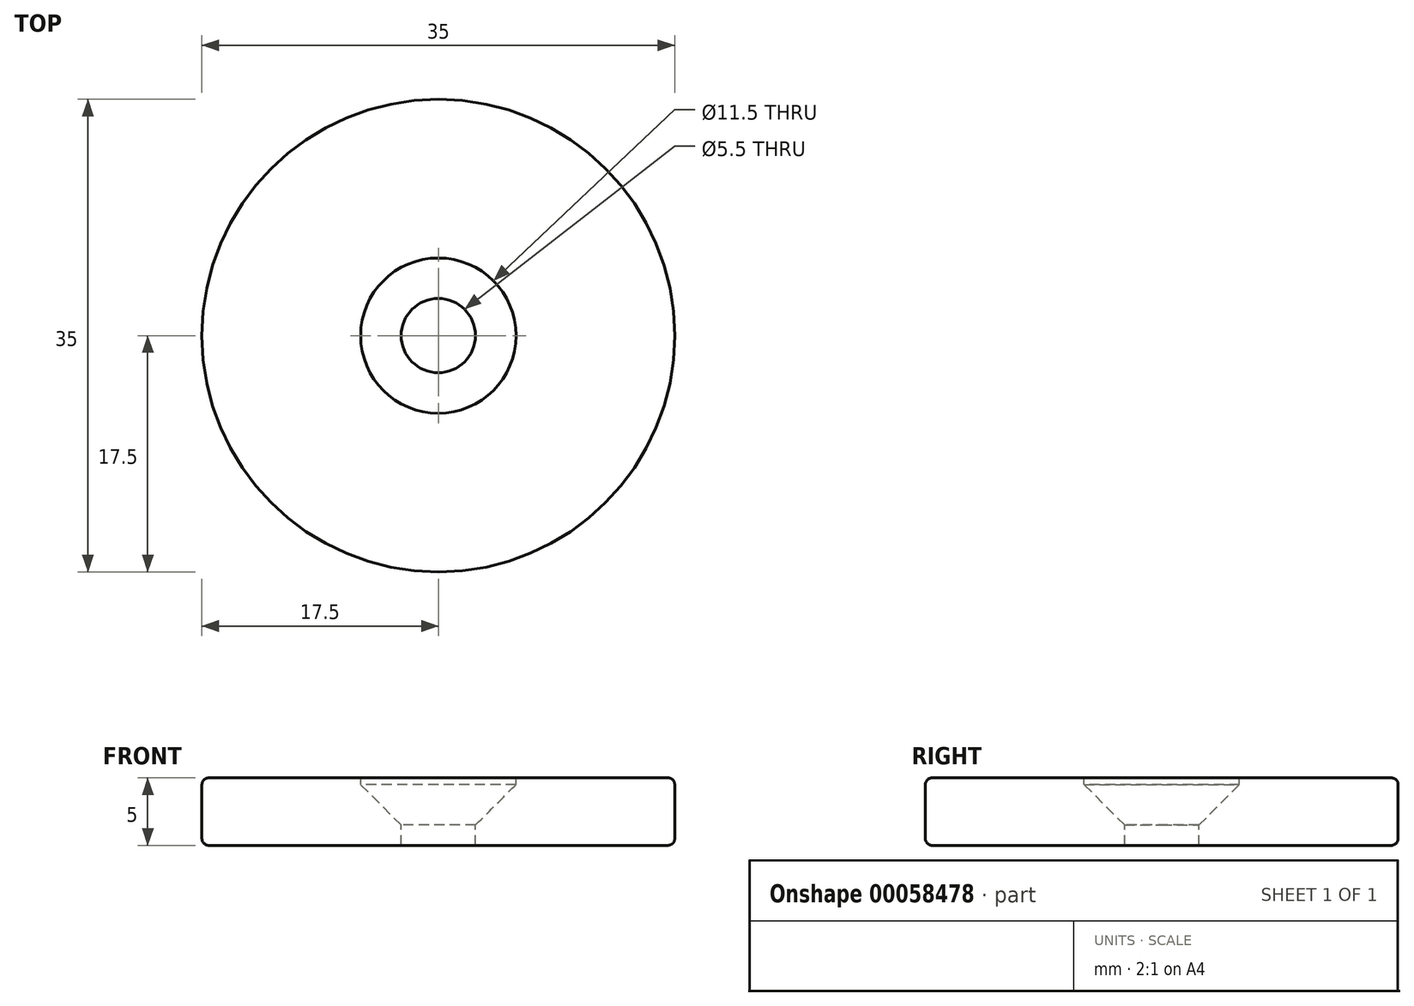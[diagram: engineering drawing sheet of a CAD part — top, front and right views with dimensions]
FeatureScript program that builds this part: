
annotation { "Feature Type Name" : "Feature", "Feature Type Description" : "" }
export const myFeature = defineFeature(function(context is Context, id is Id, definition is map)
    precondition{}
    {
        {
            var Q0;
            Q0=qCreatedBy(makeId("Top.planeOp"),FACE);
            var sketch = newSketch(context, id + "F0", { "sketchPlane" : qUnion([Q0])});
            skCircle(sketch, "E0", {"center": v(0, 0) * mm, "radius": 17.5 * mm});
            skSolve(sketch);
        }
        {
            var Q0;
            Q0 = qSketchRegion(id + "F0", true);
            extrude(context, id + "F1", {"entities" : qUnion([Q0]), "depth" : 5 * mm});
        }
        {
            var Q0;
            Q0=makeQuery(id+"F1.opExtrude","CAP_FACE",FACE,{"disambiguationData":[OSD([sQuery(id+"F0.wireOp",EDGE,"E0")])],"isStart":false});
            var sketch = newSketch(context, id + "F2", { "sketchPlane" : qUnion([Q0])});
            skCircle(sketch, "E1", {"center": v(0, 0) * mm, "radius": 5.75 * mm});
            skSolve(sketch);
        }
        {
            var Q0;
            Q0=makeQuery(id+"F2.imprint","IMPRINT",FACE,{"disambiguationData":[TD([[makeQuery(id+"F2.imprint","IMPRINT",EDGE,{"derivedFrom":sQuery(id+"F2.wireOp",EDGE,"E1")}),1.0]])]});
            extrude(context, id + "F3", {"entities" : qUnion([Q0]), "operationType" : NewBodyOperationType.REMOVE, "oppositeDirection" : true, "depth" : 0.5 * mm});
        }
        {
            var Q0;
            Q0=makeQuery(id+"F3.boolean.opBoolean","COPY",FACE,{"derivedFrom":makeQuery(id+"F3.opExtrude","CAP_FACE",FACE,{"disambiguationData":[OSD([sQuery(id+"F2.wireOp",EDGE,"E1")])],"isStart":false})});
            var sketch = newSketch(context, id + "F4", { "sketchPlane" : qUnion([Q0])});
            skPoint(sketch, "E2", {"position": v(0, 0) * mm});
            skSolve(sketch);
        }
        {
            var Q0;
            Q0=sQuery(id+"F4.wireOp",VERTEX,"E2");
            var Q1;
            Q1=makeQuery(id+"F1.opExtrude","SWEPT_BODY",BODY,{"disambiguationData":[OSD([sQuery(id+"F0.wireOp",EDGE,"E0")])]});
            hole(context, id + "F5", {"style" : HoleStyle.C_SINK, "holeDiameter" : 5.5 * mm, "cSinkDiameter" : 11.5 * mm, "endStyle" : HoleEndStyle.THROUGH, "locations" : qUnion([Q0]), "scope" : qUnion([Q1]), "cSinkAngle" : 90 * degree});
        }
        {
            var Q0;
            Q0=makeQuery(id+"F1.opExtrude","CAP_EDGE",EDGE,{"disambiguationData":[OSD([sQuery(id+"F0.wireOp",EDGE,"E0")])],"isStart":false});
            var Q1;
            Q1=makeQuery(id+"F1.opExtrude","CAP_EDGE",EDGE,{"disambiguationData":[OSD([sQuery(id+"F0.wireOp",EDGE,"E0")])],"isStart":true});
            fillet(context, id + "F6", {"entities" : qUnion([Q0, Q1]), "radius" : 0.5 * mm, "tangentPropagation" : true, "allowEdgeOverflow" : false});
        }
    });
